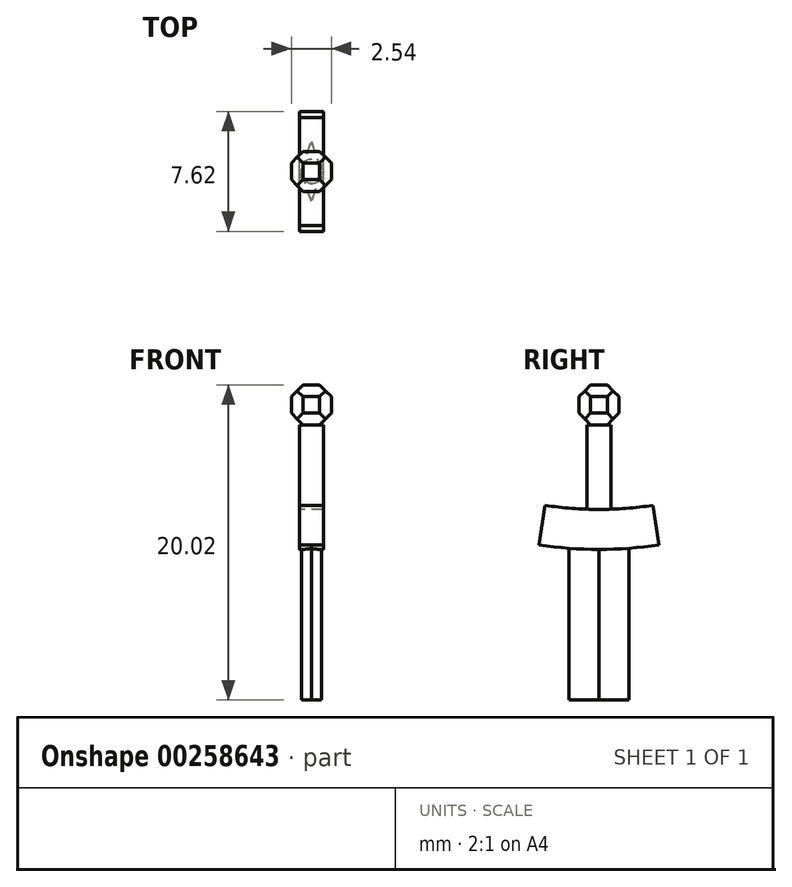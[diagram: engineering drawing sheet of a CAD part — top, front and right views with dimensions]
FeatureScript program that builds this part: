
annotation { "Feature Type Name" : "Feature", "Feature Type Description" : "" }
export const myFeature = defineFeature(function(context is Context, id is Id, definition is map)
    precondition{}
    {
        {
            var Q0;
            Q0=qCreatedBy(makeId("Top.planeOp"),FACE);
            var sketch = newSketch(context, id + "F0", { "sketchPlane" : qUnion([Q0])});
            skCircle(sketch, "E0", {"center": v(0, 0) * mm, "radius": 6.35 * mm});
            skSolve(sketch);
        }
        {
            var Q0;
            Q0=qSketchRegion(id+"F0",true);
            extrude(context, id + "F1", {"entities" : qUnion([Q0]), "depth" : 1.59 * mm});
        }
        {
            var Q0;
            Q0=makeQuery(id+"F1.opExtrude","CAP_FACE",FACE,{"disambiguationData":[OSD([sQuery(id+"F0.wireOp",EDGE,"E0")])],"isStart":false});
            var sketch = newSketch(context, id + "F2", { "sketchPlane" : qUnion([Q0])});
            skCircle(sketch, "E1", {"center": v(0, 0) * mm, "radius": 5.72 * mm});
            skCircle(sketch, "E2.0", {"center": v(0, 0) * mm, "radius": 6.35 * mm});
            skFitSpline(sketch, "E3", {"points": [v(-2.99, -3.48) * mm, v(-2.95, -3.46) * mm, v(-2.86, -3.42) * mm, v(-2.74, -3.39) * mm, v(-2.6, -3.35) * mm, v(-2.43, -3.3) * mm, v(-2.3, -3.28) * mm, v(-2.2, -3.25) * mm, v(-2.15, -3.14) * mm, v(-2.13, -3.01) * mm, v(-2.13, -2.82) * mm, v(-2.12, -2.72) * mm, v(-2.07, -2.57) * mm, v(-2, -2.44) * mm, v(-1.95, -2.43) * mm, v(-1.87, -2.47) * mm, v(-1.8, -2.57) * mm, v(-1.76, -2.65) * mm, v(-1.67, -2.67) * mm, v(-1.54, -2.67) * mm, v(-1.4, -2.63) * mm, v(-1.28, -2.57) * mm, v(-1.17, -2.5) * mm, v(-1.04, -2.4) * mm, v(-0.91, -2.23) * mm, v(-0.83, -2.05) * mm, v(-0.77, -1.87) * mm, v(-0.77, -1.6) * mm, v(-0.82, -1.35) * mm, v(-0.9, -1.14) * mm, v(-1.03, -0.9) * mm, v(-1.19, -0.72) * mm, v(-1.49, -0.53) * mm, v(-1.79, -0.45) * mm, v(-2.09, -0.45) * mm, v(-2.47, -0.46) * mm, v(-2.74, -0.46) * mm, v(-2.94, -0.5) * mm, v(-3.18, -0.62) * mm, v(-3.33, -0.78) * mm, v(-3.4, -0.96) * mm, v(-3.45, -1.13) * mm, v(-3.45, -1.23) * mm, v(-3.5, -1.37) * mm, v(-3.57, -1.5) * mm, v(-3.61, -1.59) * mm, v(-3.6, -1.65) * mm, v(-3.56, -1.72) * mm, v(-3.53, -1.77) * mm, v(-3.51, -1.85) * mm, v(-3.57, -1.93) * mm, v(-3.6, -1.96) * mm, v(-3.66, -2) * mm, v(-3.66, -2.01) * mm, v(-3.67, -2.03) * mm, v(-3.66, -2.05) * mm, v(-3.65, -2.07) * mm, v(-3.63, -2.09) * mm, v(-3.53, -2.23) * mm, v(-3.46, -2.33) * mm, v(-3.48, -2.4) * mm, v(-3.54, -2.44) * mm, v(-3.6, -2.48) * mm, v(-3.61, -2.49) * mm, v(-3.6, -2.5) * mm, v(-3.57, -2.52) * mm, v(-3.56, -2.54) * mm, v(-3.57, -2.57) * mm, v(-3.6, -2.6) * mm, v(-3.65, -2.66) * mm, v(-3.66, -2.72) * mm, v(-3.59, -2.76) * mm, v(-3.44, -2.8) * mm, v(-3.3, -2.78) * mm, v(-3.16, -2.74) * mm, v(-3.02, -2.7) * mm, v(-2.86, -2.69) * mm, v(-2.77, -2.7) * mm, v(-2.74, -2.74) * mm, v(-2.73, -2.81) * mm, v(-2.74, -2.88) * mm, v(-2.78, -2.96) * mm, v(-2.92, -3) * mm, v(-3, -3.03) * mm, v(-3.1, -3.05) * mm, v(-3.29, -3.07) * mm, v(-3.43, -3.07) * mm, v(-3.55, -3.04) * mm, v(-3.62, -3.03) * mm, v(-3.64, -3.06) * mm, v(-3.59, -3.13) * mm, v(-3.56, -3.22) * mm, v(-3.58, -3.3) * mm, v(-3.6, -3.39) * mm, v(-3.6, -3.5) * mm, v(-3.52, -3.56) * mm, v(-3.18, -3.57) * mm, v(-2.99, -3.48) * mm]});
            skFitSpline(sketch, "E4", {"points": [v(-3.38, -1.71) * mm, v(-3.39, -1.8) * mm, v(-3.34, -1.88) * mm, v(-3.3, -1.95) * mm, v(-3.3, -2.01) * mm, v(-3.3, -2.06) * mm, v(-3.26, -2.12) * mm, v(-3.17, -2.1) * mm, v(-3.11, -2) * mm, v(-3.11, -1.92) * mm, v(-3.13, -1.84) * mm, v(-3.19, -1.76) * mm, v(-3.25, -1.72) * mm, v(-3.32, -1.7) * mm, v(-3.38, -1.71) * mm]});
            skLineSegment(sketch, "E5", {"start": v(-3.52, -2.83) * mm, "end": v(-3.52, -2.9) * mm});
            skLineSegment(sketch, "E6", {"start": v(-3.52, -2.9) * mm, "end": v(-3.44, -2.92) * mm});
            skLineSegment(sketch, "E7", {"start": v(-3.44, -2.92) * mm, "end": v(-3.44, -2.85) * mm});
            skLineSegment(sketch, "E8", {"start": v(-3.44, -2.85) * mm, "end": v(-3.52, -2.83) * mm});
            skLineSegment(sketch, "E9", {"start": v(-3.41, -2.85) * mm, "end": v(-3.41, -2.92) * mm});
            skLineSegment(sketch, "E10", {"start": v(-3.41, -2.92) * mm, "end": v(-3.33, -2.92) * mm});
            skLineSegment(sketch, "E11", {"start": v(-3.33, -2.92) * mm, "end": v(-3.33, -2.85) * mm});
            skLineSegment(sketch, "E12", {"start": v(-3.33, -2.85) * mm, "end": v(-3.41, -2.85) * mm});
            skLineSegment(sketch, "E13", {"start": v(-3.3, -2.85) * mm, "end": v(-3.3, -2.92) * mm});
            skLineSegment(sketch, "E14", {"start": v(-3.3, -2.92) * mm, "end": v(-3.22, -2.92) * mm});
            skLineSegment(sketch, "E15", {"start": v(-3.22, -2.92) * mm, "end": v(-3.23, -2.84) * mm});
            skLineSegment(sketch, "E16", {"start": v(-3.23, -2.84) * mm, "end": v(-3.3, -2.85) * mm});
            skLineSegment(sketch, "E17", {"start": v(-3.2, -2.83) * mm, "end": v(-3.2, -2.92) * mm});
            skLineSegment(sketch, "E18", {"start": v(-3.2, -2.92) * mm, "end": v(-3.12, -2.9) * mm});
            skLineSegment(sketch, "E19", {"start": v(-3.12, -2.9) * mm, "end": v(-3.12, -2.81) * mm});
            skLineSegment(sketch, "E20", {"start": v(-3.12, -2.81) * mm, "end": v(-3.2, -2.83) * mm});
            skLineSegment(sketch, "E21", {"start": v(-3.09, -2.8) * mm, "end": v(-3.09, -2.9) * mm});
            skLineSegment(sketch, "E22", {"start": v(-3.09, -2.9) * mm, "end": v(-3, -2.87) * mm});
            skLineSegment(sketch, "E23", {"start": v(-3, -2.87) * mm, "end": v(-3, -2.77) * mm});
            skLineSegment(sketch, "E24", {"start": v(-3, -2.77) * mm, "end": v(-3.09, -2.8) * mm});
            skLineSegment(sketch, "E25", {"start": v(-2.98, -2.75) * mm, "end": v(-2.98, -2.86) * mm});
            skLineSegment(sketch, "E26", {"start": v(-2.98, -2.86) * mm, "end": v(-2.9, -2.83) * mm});
            skLineSegment(sketch, "E27", {"start": v(-2.9, -2.83) * mm, "end": v(-2.9, -2.73) * mm});
            skLineSegment(sketch, "E28", {"start": v(-2.9, -2.73) * mm, "end": v(-2.98, -2.75) * mm});
            skLineSegment(sketch, "E29", {"start": v(-2.87, -2.72) * mm, "end": v(-2.87, -2.81) * mm});
            skLineSegment(sketch, "E30", {"start": v(-2.87, -2.81) * mm, "end": v(-2.77, -2.77) * mm});
            skLineSegment(sketch, "E31", {"start": v(-2.77, -2.8) * mm, "end": v(-2.88, -2.85) * mm});
            skLineSegment(sketch, "E32", {"start": v(-2.88, -2.85) * mm, "end": v(-2.88, -2.94) * mm});
            skLineSegment(sketch, "E33", {"start": v(-2.9, -2.95) * mm, "end": v(-2.9, -2.87) * mm});
            skLineSegment(sketch, "E34", {"start": v(-2.9, -2.87) * mm, "end": v(-2.98, -2.9) * mm});
            skLineSegment(sketch, "E35", {"start": v(-2.98, -2.9) * mm, "end": v(-2.98, -2.97) * mm});
            skLineSegment(sketch, "E36", {"start": v(-2.98, -2.97) * mm, "end": v(-2.9, -2.95) * mm});
            skLineSegment(sketch, "E37", {"start": v(-3, -2.9) * mm, "end": v(-3.09, -2.92) * mm});
            skPoint(sketch, "E37.startSnap0", {"position": v(-3.16, -2.9) * mm});
            skLineSegment(sketch, "E38", {"start": v(-3.09, -2.92) * mm, "end": v(-3.09, -3) * mm});
            skLineSegment(sketch, "E39", {"start": v(-3.09, -3) * mm, "end": v(-3, -2.98) * mm});
            skLineSegment(sketch, "E40", {"start": v(-3, -2.98) * mm, "end": v(-3, -2.9) * mm});
            skLineSegment(sketch, "E41", {"start": v(-3.12, -2.94) * mm, "end": v(-3.2, -2.95) * mm});
            skLineSegment(sketch, "E42", {"start": v(-3.2, -2.95) * mm, "end": v(-3.2, -3.02) * mm});
            skLineSegment(sketch, "E43", {"start": v(-3.2, -3.02) * mm, "end": v(-3.12, -3.01) * mm});
            skLineSegment(sketch, "E44", {"start": v(-3.12, -3.01) * mm, "end": v(-3.12, -2.94) * mm});
            skLineSegment(sketch, "E45", {"start": v(-3.23, -2.95) * mm, "end": v(-3.3, -2.95) * mm});
            skLineSegment(sketch, "E46", {"start": v(-3.3, -2.95) * mm, "end": v(-3.3, -3.03) * mm});
            skLineSegment(sketch, "E47", {"start": v(-3.3, -3.03) * mm, "end": v(-3.23, -3.03) * mm});
            skLineSegment(sketch, "E48", {"start": v(-3.23, -3.03) * mm, "end": v(-3.23, -2.95) * mm});
            skLineSegment(sketch, "E49", {"start": v(-3.33, -2.95) * mm, "end": v(-3.41, -2.95) * mm});
            skLineSegment(sketch, "E50", {"start": v(-3.41, -2.95) * mm, "end": v(-3.41, -3.02) * mm});
            skLineSegment(sketch, "E51", {"start": v(-3.41, -3.02) * mm, "end": v(-3.33, -3.03) * mm});
            skLineSegment(sketch, "E52", {"start": v(-3.33, -3.03) * mm, "end": v(-3.33, -2.95) * mm});
            skLineSegment(sketch, "E53", {"start": v(-3.52, -2.94) * mm, "end": v(-3.44, -2.95) * mm});
            skLineSegment(sketch, "E54", {"start": v(-3.44, -2.95) * mm, "end": v(-3.44, -3.01) * mm});
            skLineSegment(sketch, "E55", {"start": v(-3.44, -3.01) * mm, "end": v(-3.52, -3) * mm});
            skLineSegment(sketch, "E56", {"start": v(-3.52, -3) * mm, "end": v(-3.52, -2.94) * mm});
            skLineSegment(sketch, "E57", {"start": v(-3.64, -2.91) * mm, "end": v(-3.55, -2.94) * mm});
            skLineSegment(sketch, "E58", {"start": v(-3.55, -2.94) * mm, "end": v(-3.55, -3) * mm});
            skLineSegment(sketch, "E59", {"start": v(-3.55, -2.82) * mm, "end": v(-3.55, -2.9) * mm});
            skLineSegment(sketch, "E60", {"start": v(-3.55, -2.9) * mm, "end": v(-3.64, -2.88) * mm});
            skArc(sketch, "E61", {"start": v(-3.55, -2.82) * mm, "mid": v(-3.61, -2.82) * mm, "end": v(-3.64, -2.88) * mm});
            skArc(sketch, "E62", {"start": v(-3.64, -2.91) * mm, "mid": v(-3.61, -2.97) * mm, "end": v(-3.55, -3) * mm});
            skArc(sketch, "E63", {"start": v(-2.77, -2.77) * mm, "mid": v(-2.82, -2.73) * mm, "end": v(-2.87, -2.72) * mm});
            skArc(sketch, "E64", {"start": v(-2.88, -2.94) * mm, "mid": v(-2.8, -2.9) * mm, "end": v(-2.77, -2.8) * mm});
            skFitSpline(sketch, "E65", {"points": [v(2.09, -3.54) * mm, v(2.12, -3.52) * mm, v(2.21, -3.48) * mm, v(2.33, -3.45) * mm, v(2.46, -3.4) * mm, v(2.64, -3.36) * mm, v(2.76, -3.34) * mm, v(2.87, -3.3) * mm, v(2.92, -3.2) * mm, v(2.94, -3.08) * mm, v(2.95, -2.88) * mm, v(2.95, -2.78) * mm, v(3, -2.63) * mm, v(3.08, -2.5) * mm, v(3.13, -2.5) * mm, v(3.2, -2.53) * mm, v(3.27, -2.64) * mm, v(3.31, -2.71) * mm, v(3.4, -2.74) * mm, v(3.53, -2.74) * mm, v(3.67, -2.69) * mm, v(3.8, -2.63) * mm, v(3.9, -2.56) * mm, v(4.03, -2.46) * mm, v(4.16, -2.29) * mm, v(4.24, -2.1) * mm, v(4.3, -1.94) * mm, v(4.3, -1.66) * mm, v(4.25, -1.41) * mm, v(4.18, -1.2) * mm, v(4.04, -0.96) * mm, v(3.89, -0.78) * mm, v(3.58, -0.6) * mm, v(3.29, -0.51) * mm, v(2.97, -0.48) * mm, v(2.59, -0.52) * mm, v(2.33, -0.52) * mm, v(2.13, -0.57) * mm, v(1.9, -0.68) * mm, v(1.74, -0.84) * mm, v(1.67, -1.02) * mm, v(1.62, -1.2) * mm, v(1.63, -1.3) * mm, v(1.57, -1.43) * mm, v(1.5, -1.57) * mm, v(1.46, -1.65) * mm, v(1.46, -1.71) * mm, v(1.51, -1.78) * mm, v(1.54, -1.83) * mm, v(1.56, -1.91) * mm, v(1.5, -1.99) * mm, v(1.46, -2.02) * mm, v(1.41, -2.06) * mm, v(1.4, -2.08) * mm, v(1.4, -2.1) * mm, v(1.4, -2.11) * mm, v(1.42, -2.13) * mm, v(1.44, -2.15) * mm, v(1.54, -2.3) * mm, v(1.61, -2.4) * mm, v(1.6, -2.46) * mm, v(1.53, -2.5) * mm, v(1.47, -2.54) * mm, v(1.46, -2.55) * mm, v(1.48, -2.56) * mm, v(1.5, -2.58) * mm, v(1.52, -2.6) * mm, v(1.5, -2.63) * mm, v(1.47, -2.67) * mm, v(1.43, -2.72) * mm, v(1.41, -2.78) * mm, v(1.49, -2.82) * mm, v(1.63, -2.85) * mm, v(1.77, -2.85) * mm, v(1.91, -2.8) * mm, v(2.05, -2.77) * mm, v(2.21, -2.75) * mm, v(2.3, -2.77) * mm, v(2.33, -2.8) * mm, v(2.35, -2.88) * mm, v(2.33, -2.95) * mm, v(2.29, -3.02) * mm, v(2.15, -3.07) * mm, v(2.07, -3.09) * mm, v(1.97, -3.11) * mm, v(1.79, -3.14) * mm, v(1.64, -3.13) * mm, v(1.52, -3.1) * mm, v(1.45, -3.1) * mm, v(1.43, -3.13) * mm, v(1.48, -3.2) * mm, v(1.51, -3.28) * mm, v(1.5, -3.36) * mm, v(1.48, -3.45) * mm, v(1.48, -3.56) * mm, v(1.55, -3.62) * mm, v(1.9, -3.63) * mm, v(2.09, -3.54) * mm]});
            skFitSpline(sketch, "E66", {"points": [v(1.7, -1.77) * mm, v(1.69, -1.86) * mm, v(1.73, -1.95) * mm, v(1.78, -2) * mm, v(1.78, -2.08) * mm, v(1.76, -2.13) * mm, v(1.8, -2.19) * mm, v(1.9, -2.17) * mm, v(1.96, -2.07) * mm, v(1.96, -1.98) * mm, v(1.95, -1.9) * mm, v(1.88, -1.82) * mm, v(1.82, -1.78) * mm, v(1.75, -1.76) * mm, v(1.7, -1.77) * mm]});
            skLineSegment(sketch, "E67", {"start": v(1.55, -2.9) * mm, "end": v(1.55, -2.97) * mm});
            skLineSegment(sketch, "E68", {"start": v(1.55, -2.97) * mm, "end": v(1.63, -2.98) * mm});
            skLineSegment(sketch, "E69", {"start": v(1.63, -2.98) * mm, "end": v(1.63, -2.9) * mm});
            skLineSegment(sketch, "E70", {"start": v(1.63, -2.9) * mm, "end": v(1.55, -2.9) * mm});
            skLineSegment(sketch, "E71", {"start": v(1.66, -2.91) * mm, "end": v(1.66, -2.98) * mm});
            skLineSegment(sketch, "E72", {"start": v(1.66, -2.98) * mm, "end": v(1.74, -2.98) * mm});
            skLineSegment(sketch, "E73", {"start": v(1.74, -2.98) * mm, "end": v(1.74, -2.92) * mm});
            skLineSegment(sketch, "E74", {"start": v(1.74, -2.92) * mm, "end": v(1.66, -2.91) * mm});
            skLineSegment(sketch, "E75", {"start": v(1.77, -2.91) * mm, "end": v(1.77, -2.98) * mm});
            skLineSegment(sketch, "E76", {"start": v(1.77, -2.98) * mm, "end": v(1.85, -2.98) * mm});
            skLineSegment(sketch, "E77", {"start": v(1.85, -2.98) * mm, "end": v(1.85, -2.9) * mm});
            skLineSegment(sketch, "E78", {"start": v(1.85, -2.9) * mm, "end": v(1.77, -2.91) * mm});
            skLineSegment(sketch, "E79", {"start": v(1.88, -2.9) * mm, "end": v(1.88, -2.98) * mm});
            skLineSegment(sketch, "E80", {"start": v(1.88, -2.98) * mm, "end": v(1.95, -2.96) * mm});
            skLineSegment(sketch, "E81", {"start": v(1.95, -2.96) * mm, "end": v(1.95, -2.88) * mm});
            skLineSegment(sketch, "E82", {"start": v(1.95, -2.88) * mm, "end": v(1.88, -2.9) * mm});
            skLineSegment(sketch, "E83", {"start": v(1.99, -2.86) * mm, "end": v(1.99, -2.96) * mm});
            skLineSegment(sketch, "E84", {"start": v(1.99, -2.96) * mm, "end": v(2.07, -2.93) * mm});
            skLineSegment(sketch, "E85", {"start": v(2.07, -2.93) * mm, "end": v(2.07, -2.83) * mm});
            skLineSegment(sketch, "E86", {"start": v(2.07, -2.83) * mm, "end": v(1.99, -2.86) * mm});
            skLineSegment(sketch, "E87", {"start": v(2.1, -2.82) * mm, "end": v(2.1, -2.92) * mm});
            skLineSegment(sketch, "E88", {"start": v(2.1, -2.92) * mm, "end": v(2.17, -2.9) * mm});
            skLineSegment(sketch, "E89", {"start": v(2.17, -2.9) * mm, "end": v(2.17, -2.8) * mm});
            skLineSegment(sketch, "E90", {"start": v(2.17, -2.8) * mm, "end": v(2.1, -2.82) * mm});
            skLineSegment(sketch, "E91", {"start": v(2.2, -2.79) * mm, "end": v(2.2, -2.88) * mm});
            skLineSegment(sketch, "E92", {"start": v(2.2, -2.88) * mm, "end": v(2.3, -2.84) * mm});
            skLineSegment(sketch, "E93", {"start": v(2.3, -2.87) * mm, "end": v(2.2, -2.92) * mm});
            skLineSegment(sketch, "E94", {"start": v(2.2, -2.92) * mm, "end": v(2.2, -3) * mm});
            skLineSegment(sketch, "E95", {"start": v(2.17, -3.01) * mm, "end": v(2.17, -2.93) * mm});
            skLineSegment(sketch, "E96", {"start": v(2.17, -2.93) * mm, "end": v(2.1, -2.96) * mm});
            skLineSegment(sketch, "E97", {"start": v(2.1, -2.96) * mm, "end": v(2.1, -3.04) * mm});
            skLineSegment(sketch, "E98", {"start": v(2.1, -3.04) * mm, "end": v(2.17, -3.01) * mm});
            skLineSegment(sketch, "E99", {"start": v(2.06, -2.97) * mm, "end": v(1.98, -2.99) * mm});
            skPoint(sketch, "E99.startSnap0", {"position": v(1.91, -2.97) * mm});
            skLineSegment(sketch, "E100", {"start": v(1.98, -2.99) * mm, "end": v(1.99, -3.07) * mm});
            skLineSegment(sketch, "E101", {"start": v(1.99, -3.07) * mm, "end": v(2.07, -3.05) * mm});
            skLineSegment(sketch, "E102", {"start": v(2.07, -3.05) * mm, "end": v(2.06, -2.97) * mm});
            skLineSegment(sketch, "E103", {"start": v(1.95, -3) * mm, "end": v(1.88, -3.01) * mm});
            skLineSegment(sketch, "E104", {"start": v(1.88, -3.01) * mm, "end": v(1.88, -3.09) * mm});
            skLineSegment(sketch, "E105", {"start": v(1.88, -3.09) * mm, "end": v(1.95, -3.07) * mm});
            skLineSegment(sketch, "E106", {"start": v(1.95, -3.07) * mm, "end": v(1.95, -3) * mm});
            skLineSegment(sketch, "E107", {"start": v(1.84, -3.02) * mm, "end": v(1.77, -3.02) * mm});
            skLineSegment(sketch, "E108", {"start": v(1.77, -3.02) * mm, "end": v(1.77, -3.1) * mm});
            skLineSegment(sketch, "E109", {"start": v(1.77, -3.1) * mm, "end": v(1.85, -3.1) * mm});
            skLineSegment(sketch, "E110", {"start": v(1.85, -3.1) * mm, "end": v(1.84, -3.02) * mm});
            skLineSegment(sketch, "E111", {"start": v(1.74, -3.02) * mm, "end": v(1.66, -3.02) * mm});
            skLineSegment(sketch, "E112", {"start": v(1.66, -3.02) * mm, "end": v(1.66, -3.08) * mm});
            skLineSegment(sketch, "E113", {"start": v(1.66, -3.08) * mm, "end": v(1.74, -3.1) * mm});
            skLineSegment(sketch, "E114", {"start": v(1.74, -3.1) * mm, "end": v(1.74, -3.02) * mm});
            skLineSegment(sketch, "E115", {"start": v(1.56, -3) * mm, "end": v(1.63, -3.01) * mm});
            skLineSegment(sketch, "E116", {"start": v(1.63, -3.01) * mm, "end": v(1.63, -3.08) * mm});
            skLineSegment(sketch, "E117", {"start": v(1.63, -3.08) * mm, "end": v(1.55, -3.07) * mm});
            skLineSegment(sketch, "E118", {"start": v(1.55, -3.07) * mm, "end": v(1.56, -3) * mm});
            skLineSegment(sketch, "E119", {"start": v(1.43, -2.97) * mm, "end": v(1.52, -3) * mm});
            skLineSegment(sketch, "E120", {"start": v(1.52, -3) * mm, "end": v(1.52, -3.06) * mm});
            skLineSegment(sketch, "E121", {"start": v(1.52, -2.89) * mm, "end": v(1.52, -2.96) * mm});
            skLineSegment(sketch, "E122", {"start": v(1.52, -2.96) * mm, "end": v(1.43, -2.94) * mm});
            skArc(sketch, "E123", {"start": v(1.52, -2.89) * mm, "mid": v(1.46, -2.88) * mm, "end": v(1.43, -2.94) * mm});
            skArc(sketch, "E124", {"start": v(1.43, -2.97) * mm, "mid": v(1.46, -3.04) * mm, "end": v(1.52, -3.06) * mm});
            skArc(sketch, "E125", {"start": v(2.3, -2.84) * mm, "mid": v(2.26, -2.8) * mm, "end": v(2.2, -2.79) * mm});
            skArc(sketch, "E126", {"start": v(2.2, -3) * mm, "mid": v(2.27, -2.95) * mm, "end": v(2.3, -2.87) * mm});
            skLineSegment(sketch, "E127", {"start": v(-2.47, -0.46) * mm, "end": v(-2.47, 3.73) * mm});
            skLineSegment(sketch, "E128", {"start": v(-2.47, 3.73) * mm, "end": v(2.97, 3.73) * mm});
            skLineSegment(sketch, "E129", {"start": v(2.97, 3.73) * mm, "end": v(2.97, -0.48) * mm});
            skLineSegment(sketch, "E130", {"start": v(-2.09, -0.45) * mm, "end": v(-2.09, 3.35) * mm});
            skLineSegment(sketch, "E131", {"start": v(-2.09, 3.35) * mm, "end": v(2.59, 3.35) * mm});
            skLineSegment(sketch, "E132", {"start": v(2.59, 3.35) * mm, "end": v(2.59, -0.52) * mm});
            skSolve(sketch);
        }
        {
            var Q0;
            Q0=qSketchRegion(id+"F2",true);
            var Q1;
            Q1=makeQuery(id+"F2.imprint","IMPRINT",FACE,{"disambiguationData":[TD([[makeQuery(id+"F2.imprint","IMPRINT",EDGE,{"derivedFrom":sQuery(id+"F2.wireOp",EDGE,"8ff43451-18cf-4e1d-a6c1-207112ed4b83")}),-1.0]])]});
            var Q2;
            {var subQ0=sQuery(id+"F2.wireOp",EDGE,"f0ZndoA6-M2V5-AV1c-evuh-kt5lGmkfnjif");Q2=makeQuery(id+"F2.imprint","IMPRINT",FACE,{"disambiguationData":[TD([[makeQuery(id+"F2.imprint","IMPRINT",EDGE,{"derivedFrom":subQ0}),-1.0]])]});}
            var Q3;
            Q3=makeQuery(id+"F2.imprint","IMPRINT",FACE,{"disambiguationData":[TD([[makeQuery(id+"F2.imprint","IMPRINT",EDGE,{"derivedFrom":sQuery(id+"F2.wireOp",EDGE,"9676f148-d3db-47f1-8d18-ed8e72a81f72")}),-1.0]])]});
            var Q4;
            Q4=makeQuery(id+"F2.imprint","IMPRINT",FACE,{"disambiguationData":[TD([[makeQuery(id+"F2.imprint","IMPRINT",EDGE,{"derivedFrom":sQuery(id+"F2.wireOp",EDGE,"6HFhc678-r75o-y9sA-huqe-qlUwMVaPKWuP")}),-1.0]])]});
            var Q5;
            Q5=makeQuery(id+"F2.imprint","IMPRINT",FACE,{"disambiguationData":[TD([[makeQuery(id+"F2.imprint","IMPRINT",EDGE,{"derivedFrom":sQuery(id+"F2.wireOp",EDGE,"Xs92rVgm-BZGN-NsKB-OARH-R7qVRdKGH7H2")}),-1.0]])]});
            var Q6;
            Q6=makeQuery(id+"F2.imprint","IMPRINT",FACE,{"disambiguationData":[TD([[makeQuery(id+"F2.imprint","IMPRINT",EDGE,{"derivedFrom":sQuery(id+"F2.wireOp",EDGE,"E6WdCPIx-waOx-idA0-XJ1L-eRR6RgLmtCCS")}),-1.0]])]});
            var Q7;
            Q7=makeQuery(id+"F2.imprint","IMPRINT",FACE,{"disambiguationData":[TD([[makeQuery(id+"F2.imprint","IMPRINT",EDGE,{"derivedFrom":sQuery(id+"F2.wireOp",EDGE,"k1KiTlt2-ZZcU-dbgL-0rmk-Dgw59MTWpoCj")}),1.0]])]});
            var Q8;
            Q8=makeQuery(id+"F2.imprint","IMPRINT",FACE,{"disambiguationData":[TD([[makeQuery(id+"F2.imprint","IMPRINT",EDGE,{"derivedFrom":sQuery(id+"F2.wireOp",EDGE,"Z35Rb9R9-Rahv-nOh3-XL17-nKowExZUsZCT")}),1.0]])]});
            var Q9;
            Q9=makeQuery(id+"F2.imprint","IMPRINT",FACE,{"disambiguationData":[TD([[makeQuery(id+"F2.imprint","IMPRINT",EDGE,{"derivedFrom":sQuery(id+"F2.wireOp",EDGE,"Qg5ONqqo-2bfa-kxUG-9bmz-Wc6T9dYv9u8v")}),1.0]])]});
            var Q10;
            Q10=makeQuery(id+"F2.imprint","IMPRINT",FACE,{"disambiguationData":[TD([[makeQuery(id+"F2.imprint","IMPRINT",EDGE,{"derivedFrom":sQuery(id+"F2.wireOp",EDGE,"AjI9mxPJ-XULu-6nMp-z6qf-DJC3dJrP3SV3")}),1.0]])]});
            var Q11;
            Q11=makeQuery(id+"F2.imprint","IMPRINT",FACE,{"disambiguationData":[TD([[makeQuery(id+"F2.imprint","IMPRINT",EDGE,{"derivedFrom":sQuery(id+"F2.wireOp",EDGE,"SVXRag1M-qj8O-Xghp-BRg2-clQjxRkFYdgi")}),1.0]])]});
            var Q12;
            Q12=makeQuery(id+"F2.imprint","IMPRINT",FACE,{"disambiguationData":[TD([[makeQuery(id+"F2.imprint","IMPRINT",EDGE,{"derivedFrom":sQuery(id+"F2.wireOp",EDGE,"QknCvVvT-fZar-JZdj-N9ht-K5PjY9N2CpLl")}),1.0]])]});
            var Q13;
            Q13=makeQuery(id+"F2.imprint","IMPRINT",FACE,{"disambiguationData":[TD([[makeQuery(id+"F2.imprint","IMPRINT",EDGE,{"derivedFrom":sQuery(id+"F2.wireOp",EDGE,"IwH12iTC-POgW-ZuDk-O3qY-x9Lpsw7XAAf3")}),1.0]])]});
            var Q14;
            Q14=makeQuery(id+"F2.imprint","IMPRINT",FACE,{"disambiguationData":[TD([[makeQuery(id+"F2.imprint","IMPRINT",EDGE,{"derivedFrom":sQuery(id+"F2.wireOp",EDGE,"UGZWNjaC-YJYr-0zUO-1gu3-YYbdkgLbKj1s")}),1.0]])]});
            var Q15;
            Q15=makeQuery(id+"F2.imprint","IMPRINT",FACE,{"disambiguationData":[TD([[makeQuery(id+"F2.imprint","IMPRINT",EDGE,{"derivedFrom":sQuery(id+"F2.wireOp",EDGE,"faBvcXIA-NgVa-Zogo-Hth3-byswulnYsCry")}),1.0]])]});
            var Q16;
            Q16=makeQuery(id+"F2.imprint","IMPRINT",FACE,{"disambiguationData":[TD([[makeQuery(id+"F2.imprint","IMPRINT",EDGE,{"derivedFrom":sQuery(id+"F2.wireOp",EDGE,"z3QF5KZu-mklS-Cyfl-OEiK-EEmoJCKWUvB4")}),1.0]])]});
            var Q17;
            Q17=makeQuery(id+"F2.imprint","IMPRINT",FACE,{"disambiguationData":[TD([[makeQuery(id+"F2.imprint","IMPRINT",EDGE,{"derivedFrom":sQuery(id+"F2.wireOp",EDGE,"V2NIJvH9-TtMw-qc9R-an5m-Kvf6aCU9D1Wj")}),1.0]])]});
            var Q18;
            Q18=makeQuery(id+"F2.imprint","IMPRINT",FACE,{"disambiguationData":[TD([[makeQuery(id+"F2.imprint","IMPRINT",EDGE,{"derivedFrom":sQuery(id+"F2.wireOp",EDGE,"QeDBAyft-zymL-5vx5-wYYY-tHA32UShdvIB")}),1.0]])]});
            var Q19;
            Q19=makeQuery(id+"F2.imprint","IMPRINT",FACE,{"disambiguationData":[TD([[makeQuery(id+"F2.imprint","IMPRINT",EDGE,{"derivedFrom":sQuery(id+"F2.wireOp",EDGE,"WRGg1PvO-WrmP-NIcv-oRJx-bzyG9trbOkE2")}),1.0]])]});
            var Q20;
            Q20=makeQuery(id+"F2.imprint","IMPRINT",FACE,{"disambiguationData":[TD([[makeQuery(id+"F2.imprint","IMPRINT",EDGE,{"derivedFrom":sQuery(id+"F2.wireOp",EDGE,"75ec5599-b41b-4d6a-bb06-b73393bb844d")}),-1.0]])]});
            var Q21;
            Q21=makeQuery(id+"F2.imprint","IMPRINT",FACE,{"disambiguationData":[TD([[makeQuery(id+"F2.imprint","IMPRINT",EDGE,{"derivedFrom":sQuery(id+"F2.wireOp",EDGE,"62e6d997-3ff5-4a1c-8de8-b05959ec7cbc")}),-1.0]])]});
            var Q22;
            Q22=makeQuery(id+"F2.imprint","IMPRINT",FACE,{"disambiguationData":[TD([[makeQuery(id+"F2.imprint","IMPRINT",EDGE,{"derivedFrom":sQuery(id+"F2.wireOp",EDGE,"b8f4918c-dbd8-4fdd-af15-bc96a6b6a90d")}),-1.0]])]});
            var Q23;
            Q23=makeQuery(id+"F2.imprint","IMPRINT",FACE,{"disambiguationData":[TD([[makeQuery(id+"F2.imprint","IMPRINT",EDGE,{"derivedFrom":sQuery(id+"F2.wireOp",EDGE,"337819dd-2963-4144-94d7-e260421f4e37")}),1.0]])]});
            var Q24;
            Q24=makeQuery(id+"F2.imprint","IMPRINT",FACE,{"disambiguationData":[TD([[makeQuery(id+"F2.imprint","IMPRINT",EDGE,{"derivedFrom":sQuery(id+"F2.wireOp",EDGE,"19c6ec17-bb67-46df-91db-361c1b9a8fc6")}),1.0]])]});
            var Q25;
            Q25=makeQuery(id+"F2.imprint","IMPRINT",FACE,{"disambiguationData":[TD([[makeQuery(id+"F2.imprint","IMPRINT",EDGE,{"derivedFrom":sQuery(id+"F2.wireOp",EDGE,"b55352ad-c42c-4425-987b-4bb80f046402")}),1.0]])]});
            var Q26;
            Q26=makeQuery(id+"F2.imprint","IMPRINT",FACE,{"disambiguationData":[TD([[makeQuery(id+"F2.imprint","IMPRINT",EDGE,{"derivedFrom":sQuery(id+"F2.wireOp",EDGE,"b27b330e-c63e-4a5d-9a41-1e5f11f57855")}),1.0]])]});
            var Q27;
            Q27=makeQuery(id+"F2.imprint","IMPRINT",FACE,{"disambiguationData":[TD([[makeQuery(id+"F2.imprint","IMPRINT",EDGE,{"derivedFrom":sQuery(id+"F2.wireOp",EDGE,"cd0931f7-213e-4ee0-afb0-8455a1d6fb19")}),1.0]])]});
            var Q28;
            Q28=makeQuery(id+"F2.imprint","IMPRINT",FACE,{"disambiguationData":[TD([[makeQuery(id+"F2.imprint","IMPRINT",EDGE,{"derivedFrom":sQuery(id+"F2.wireOp",EDGE,"2ee7f471-c0e9-471b-9897-f54198c6bebe")}),1.0]])]});
            var Q29;
            Q29=makeQuery(id+"F2.imprint","IMPRINT",FACE,{"disambiguationData":[TD([[makeQuery(id+"F2.imprint","IMPRINT",EDGE,{"derivedFrom":sQuery(id+"F2.wireOp",EDGE,"1a649881-7116-4bcf-9e85-0b71573aa8aa")}),1.0]])]});
            var Q30;
            Q30=makeQuery(id+"F2.imprint","IMPRINT",FACE,{"disambiguationData":[TD([[makeQuery(id+"F2.imprint","IMPRINT",EDGE,{"derivedFrom":sQuery(id+"F2.wireOp",EDGE,"c0ec6f99-1aba-4aca-9953-efef360278b0")}),1.0]])]});
            var Q31;
            Q31=makeQuery(id+"F2.imprint","IMPRINT",FACE,{"disambiguationData":[TD([[makeQuery(id+"F2.imprint","IMPRINT",EDGE,{"derivedFrom":sQuery(id+"F2.wireOp",EDGE,"17c59965-fe3a-40f4-ab79-7e7308dcb645")}),1.0]])]});
            var Q32;
            Q32=makeQuery(id+"F2.imprint","IMPRINT",FACE,{"disambiguationData":[TD([[makeQuery(id+"F2.imprint","IMPRINT",EDGE,{"derivedFrom":sQuery(id+"F2.wireOp",EDGE,"bf3a8e90-f25c-4be5-acd2-482a28ec085b")}),1.0]])]});
            var Q33;
            Q33=makeQuery(id+"F2.imprint","IMPRINT",FACE,{"disambiguationData":[TD([[makeQuery(id+"F2.imprint","IMPRINT",EDGE,{"derivedFrom":sQuery(id+"F2.wireOp",EDGE,"2cfb1138-f32f-4ed4-9923-472279ab65f4")}),1.0]])]});
            var Q34;
            Q34=makeQuery(id+"F2.imprint","IMPRINT",FACE,{"disambiguationData":[TD([[makeQuery(id+"F2.imprint","IMPRINT",EDGE,{"derivedFrom":sQuery(id+"F2.wireOp",EDGE,"cb2b1f7e-f635-4efb-b12c-495075b4995b")}),1.0]])]});
            var Q35;
            Q35=makeQuery(id+"F2.imprint","IMPRINT",FACE,{"disambiguationData":[TD([[makeQuery(id+"F2.imprint","IMPRINT",EDGE,{"derivedFrom":sQuery(id+"F2.wireOp",EDGE,"fe9d17d4-f2a5-44d9-8164-3530e82dfe4b")}),1.0]])]});
            var Q36;
            Q36=makeQuery(id+"F2.imprint","IMPRINT",FACE,{"disambiguationData":[TD([[makeQuery(id+"F2.imprint","IMPRINT",EDGE,{"derivedFrom":sQuery(id+"F2.wireOp",EDGE,"E66")}),-1.0]])]});
            var Q37;
            Q37=makeQuery(id+"F2.imprint","IMPRINT",FACE,{"disambiguationData":[TD([[makeQuery(id+"F2.imprint","IMPRINT",EDGE,{"derivedFrom":sQuery(id+"F2.wireOp",EDGE,"E4")}),-1.0]])]});
            var Q38;
            {var subQ0=sQuery(id+"F2.wireOp",EDGE,"E127");Q38=makeQuery(id+"F2.imprint","IMPRINT",FACE,{"disambiguationData":[TD([[makeQuery(id+"F2.imprint","IMPRINT",EDGE,{"derivedFrom":subQ0}),-1.0]])]});}
            var Q39;
            Q39=makeQuery(id+"F2.imprint","IMPRINT",FACE,{"disambiguationData":[TD([[makeQuery(id+"F2.imprint","IMPRINT",EDGE,{"derivedFrom":sQuery(id+"F2.wireOp",EDGE,"E59")}),-1.0]])]});
            var Q40;
            Q40=makeQuery(id+"F2.imprint","IMPRINT",FACE,{"disambiguationData":[TD([[makeQuery(id+"F2.imprint","IMPRINT",EDGE,{"derivedFrom":sQuery(id+"F2.wireOp",EDGE,"E57")}),-1.0]])]});
            var Q41;
            Q41=makeQuery(id+"F2.imprint","IMPRINT",FACE,{"disambiguationData":[TD([[makeQuery(id+"F2.imprint","IMPRINT",EDGE,{"derivedFrom":sQuery(id+"F2.wireOp",EDGE,"E53")}),-1.0]])]});
            var Q42;
            Q42=makeQuery(id+"F2.imprint","IMPRINT",FACE,{"disambiguationData":[TD([[makeQuery(id+"F2.imprint","IMPRINT",EDGE,{"derivedFrom":sQuery(id+"F2.wireOp",EDGE,"E5")}),1.0]])]});
            var Q43;
            Q43=makeQuery(id+"F2.imprint","IMPRINT",FACE,{"disambiguationData":[TD([[makeQuery(id+"F2.imprint","IMPRINT",EDGE,{"derivedFrom":sQuery(id+"F2.wireOp",EDGE,"E9")}),1.0]])]});
            var Q44;
            Q44=makeQuery(id+"F2.imprint","IMPRINT",FACE,{"disambiguationData":[TD([[makeQuery(id+"F2.imprint","IMPRINT",EDGE,{"derivedFrom":sQuery(id+"F2.wireOp",EDGE,"E49")}),1.0]])]});
            var Q45;
            Q45=makeQuery(id+"F2.imprint","IMPRINT",FACE,{"disambiguationData":[TD([[makeQuery(id+"F2.imprint","IMPRINT",EDGE,{"derivedFrom":sQuery(id+"F2.wireOp",EDGE,"E45")}),1.0]])]});
            var Q46;
            Q46=makeQuery(id+"F2.imprint","IMPRINT",FACE,{"disambiguationData":[TD([[makeQuery(id+"F2.imprint","IMPRINT",EDGE,{"derivedFrom":sQuery(id+"F2.wireOp",EDGE,"E13")}),1.0]])]});
            var Q47;
            Q47=makeQuery(id+"F2.imprint","IMPRINT",FACE,{"disambiguationData":[TD([[makeQuery(id+"F2.imprint","IMPRINT",EDGE,{"derivedFrom":sQuery(id+"F2.wireOp",EDGE,"E17")}),1.0]])]});
            var Q48;
            Q48=makeQuery(id+"F2.imprint","IMPRINT",FACE,{"disambiguationData":[TD([[makeQuery(id+"F2.imprint","IMPRINT",EDGE,{"derivedFrom":sQuery(id+"F2.wireOp",EDGE,"E41")}),1.0]])]});
            var Q49;
            Q49=makeQuery(id+"F2.imprint","IMPRINT",FACE,{"disambiguationData":[TD([[makeQuery(id+"F2.imprint","IMPRINT",EDGE,{"derivedFrom":sQuery(id+"F2.wireOp",EDGE,"E37")}),1.0]])]});
            var Q50;
            Q50=makeQuery(id+"F2.imprint","IMPRINT",FACE,{"disambiguationData":[TD([[makeQuery(id+"F2.imprint","IMPRINT",EDGE,{"derivedFrom":sQuery(id+"F2.wireOp",EDGE,"E21")}),1.0]])]});
            var Q51;
            Q51=makeQuery(id+"F2.imprint","IMPRINT",FACE,{"disambiguationData":[TD([[makeQuery(id+"F2.imprint","IMPRINT",EDGE,{"derivedFrom":sQuery(id+"F2.wireOp",EDGE,"E25")}),1.0]])]});
            var Q52;
            Q52=makeQuery(id+"F2.imprint","IMPRINT",FACE,{"disambiguationData":[TD([[makeQuery(id+"F2.imprint","IMPRINT",EDGE,{"derivedFrom":sQuery(id+"F2.wireOp",EDGE,"E33")}),1.0]])]});
            var Q53;
            Q53=makeQuery(id+"F2.imprint","IMPRINT",FACE,{"disambiguationData":[TD([[makeQuery(id+"F2.imprint","IMPRINT",EDGE,{"derivedFrom":sQuery(id+"F2.wireOp",EDGE,"E31")}),1.0]])]});
            var Q54;
            Q54=makeQuery(id+"F2.imprint","IMPRINT",FACE,{"disambiguationData":[TD([[makeQuery(id+"F2.imprint","IMPRINT",EDGE,{"derivedFrom":sQuery(id+"F2.wireOp",EDGE,"E29")}),1.0]])]});
            var Q55;
            Q55=makeQuery(id+"F2.imprint","IMPRINT",FACE,{"disambiguationData":[TD([[makeQuery(id+"F2.imprint","IMPRINT",EDGE,{"derivedFrom":sQuery(id+"F2.wireOp",EDGE,"E91")}),1.0]])]});
            var Q56;
            Q56=makeQuery(id+"F2.imprint","IMPRINT",FACE,{"disambiguationData":[TD([[makeQuery(id+"F2.imprint","IMPRINT",EDGE,{"derivedFrom":sQuery(id+"F2.wireOp",EDGE,"E93")}),1.0]])]});
            var Q57;
            Q57=makeQuery(id+"F2.imprint","IMPRINT",FACE,{"disambiguationData":[TD([[makeQuery(id+"F2.imprint","IMPRINT",EDGE,{"derivedFrom":sQuery(id+"F2.wireOp",EDGE,"E95")}),1.0]])]});
            var Q58;
            Q58=makeQuery(id+"F2.imprint","IMPRINT",FACE,{"disambiguationData":[TD([[makeQuery(id+"F2.imprint","IMPRINT",EDGE,{"derivedFrom":sQuery(id+"F2.wireOp",EDGE,"E87")}),1.0]])]});
            var Q59;
            Q59=makeQuery(id+"F2.imprint","IMPRINT",FACE,{"disambiguationData":[TD([[makeQuery(id+"F2.imprint","IMPRINT",EDGE,{"derivedFrom":sQuery(id+"F2.wireOp",EDGE,"E83")}),1.0]])]});
            var Q60;
            Q60=makeQuery(id+"F2.imprint","IMPRINT",FACE,{"disambiguationData":[TD([[makeQuery(id+"F2.imprint","IMPRINT",EDGE,{"derivedFrom":sQuery(id+"F2.wireOp",EDGE,"E99")}),1.0]])]});
            var Q61;
            Q61=makeQuery(id+"F2.imprint","IMPRINT",FACE,{"disambiguationData":[TD([[makeQuery(id+"F2.imprint","IMPRINT",EDGE,{"derivedFrom":sQuery(id+"F2.wireOp",EDGE,"E103")}),1.0]])]});
            var Q62;
            Q62=makeQuery(id+"F2.imprint","IMPRINT",FACE,{"disambiguationData":[TD([[makeQuery(id+"F2.imprint","IMPRINT",EDGE,{"derivedFrom":sQuery(id+"F2.wireOp",EDGE,"E79")}),1.0]])]});
            var Q63;
            Q63=makeQuery(id+"F2.imprint","IMPRINT",FACE,{"disambiguationData":[TD([[makeQuery(id+"F2.imprint","IMPRINT",EDGE,{"derivedFrom":sQuery(id+"F2.wireOp",EDGE,"E75")}),1.0]])]});
            var Q64;
            Q64=makeQuery(id+"F2.imprint","IMPRINT",FACE,{"disambiguationData":[TD([[makeQuery(id+"F2.imprint","IMPRINT",EDGE,{"derivedFrom":sQuery(id+"F2.wireOp",EDGE,"E107")}),1.0]])]});
            var Q65;
            Q65=makeQuery(id+"F2.imprint","IMPRINT",FACE,{"disambiguationData":[TD([[makeQuery(id+"F2.imprint","IMPRINT",EDGE,{"derivedFrom":sQuery(id+"F2.wireOp",EDGE,"E111")}),1.0]])]});
            var Q66;
            Q66=makeQuery(id+"F2.imprint","IMPRINT",FACE,{"disambiguationData":[TD([[makeQuery(id+"F2.imprint","IMPRINT",EDGE,{"derivedFrom":sQuery(id+"F2.wireOp",EDGE,"E71")}),1.0]])]});
            var Q67;
            Q67=makeQuery(id+"F2.imprint","IMPRINT",FACE,{"disambiguationData":[TD([[makeQuery(id+"F2.imprint","IMPRINT",EDGE,{"derivedFrom":sQuery(id+"F2.wireOp",EDGE,"E67")}),1.0]])]});
            var Q68;
            Q68=makeQuery(id+"F2.imprint","IMPRINT",FACE,{"disambiguationData":[TD([[makeQuery(id+"F2.imprint","IMPRINT",EDGE,{"derivedFrom":sQuery(id+"F2.wireOp",EDGE,"E115")}),-1.0]])]});
            var Q69;
            Q69=makeQuery(id+"F2.imprint","IMPRINT",FACE,{"disambiguationData":[TD([[makeQuery(id+"F2.imprint","IMPRINT",EDGE,{"derivedFrom":sQuery(id+"F2.wireOp",EDGE,"E119")}),-1.0]])]});
            var Q70;
            Q70=makeQuery(id+"F2.imprint","IMPRINT",FACE,{"disambiguationData":[TD([[makeQuery(id+"F2.imprint","IMPRINT",EDGE,{"derivedFrom":sQuery(id+"F2.wireOp",EDGE,"E121")}),-1.0]])]});
            extrude(context, id + "F3", {"entities" : qUnion([Q0, Q1, Q2, Q3, Q4, Q5, Q6, Q7, Q8, Q9, Q10, Q11, Q12, Q13, Q14, Q15, Q16, Q17, Q18, Q19, Q20, Q21, Q22, Q23, Q24, Q25, Q26, Q27, Q28, Q29, Q30, Q31, Q32, Q33, Q34, Q35, Q36, Q37, Q38, Q39, Q40, Q41, Q42, Q43, Q44, Q45, Q46, Q47, Q48, Q49, Q50, Q51, Q52, Q53, Q54, Q55, Q56, Q57, Q58, Q59, Q60, Q61, Q62, Q63, Q64, Q65, Q66, Q67, Q68, Q69, Q70]), "operationType" : NewBodyOperationType.ADD, "depth" : 0.8 * mm});
        }
        {
            var Q0;
            Q0=makeQuery(id+"F3.boolean.opBoolean","SPLIT",FACE,{"disambiguationData":[TD([makeQuery(id+"F3.opExtrude","SWEPT_FACE",FACE,{"disambiguationData":[OSD([sQuery(id+"F2.wireOp",EDGE,"E1")])]})])],"derivedFrom":makeQuery(id+"F1.opExtrude","CAP_FACE",FACE,{"disambiguationData":[OSD([sQuery(id+"F0.wireOp",EDGE,"E0")])],"isStart":false})});
            var sketch = newSketch(context, id + "F4", { "sketchPlane" : qUnion([Q0])});
            skLineSegment(sketch, "E133", {"start": v(0, 1.9) * mm, "end": v(-0.64, 0) * mm});
            skLineSegment(sketch, "E134", {"start": v(-0.64, 0) * mm, "end": v(0, -1.9) * mm});
            skLineSegment(sketch, "E135", {"start": v(0, -1.9) * mm, "end": v(0.64, 0) * mm});
            skLineSegment(sketch, "E136", {"start": v(0.64, 0) * mm, "end": v(0, 1.9) * mm});
            skSolve(sketch);
        }
        {
            var Q0;
            Q0=qSketchRegion(id+"F4",true);
            extrude(context, id + "F5", {"entities" : qUnion([Q0]), "operationType" : NewBodyOperationType.ADD, "depth" : 12.7 * mm});
        }
        {
            var Q0;
            Q0=qCreatedBy(makeId("Right.planeOp"),FACE);
            var sketch = newSketch(context, id + "F6", { "sketchPlane" : qUnion([Q0])});
            skArc(sketch, "E137", {"start": v(3.8, 13.97) * mm, "mid": v(0, 13.68) * mm, "end": v(-3.8, 13.97) * mm});
            skArc(sketch, "E138.0", {"start": v(3.43, 16.48) * mm, "mid": v(0, 16.22) * mm, "end": v(-3.43, 16.48) * mm});
            skLineSegment(sketch, "E139", {"start": v(3.8, 13.97) * mm, "end": v(3.43, 16.48) * mm});
            skLineSegment(sketch, "E140", {"start": v(-3.43, 16.48) * mm, "end": v(-3.8, 13.97) * mm});
            skSolve(sketch);
        }
        {
            var Q0;
            Q0=qSketchRegion(id+"F6",true);
            extrude(context, id + "F7", {"entities" : qUnion([Q0]), "operationType" : NewBodyOperationType.ADD, "endBound" : BoundingType.SYMMETRIC, "depth" : 1.52 * mm});
        }
        {
            var Q0;
            Q0=qCreatedBy(makeId("Right.planeOp"),FACE);
            var sketch = newSketch(context, id + "F8", { "sketchPlane" : qUnion([Q0])});
            skLineSegment(sketch, "E141", {"start": v(0, 13.97) * mm, "end": v(0, 21.6) * mm});
            skLineSegment(sketch, "E142", {"start": v(0, 21.6) * mm, "end": v(0.76, 21.6) * mm});
            skLineSegment(sketch, "E143", {"start": v(0.76, 21.6) * mm, "end": v(0.76, 13.97) * mm});
            skLineSegment(sketch, "E144", {"start": v(0.76, 13.97) * mm, "end": v(0, 13.97) * mm});
            skSolve(sketch);
        }
        {
            var Q0;
            Q0=qSketchRegion(id+"F8",true);
            var Q1;
            Q1=sQuery(id+"F8.wireOp",EDGE,"E141");
            revolve(context, id + "F9", {"operationType" : NewBodyOperationType.ADD, "entities" : qUnion([Q0]), "axis" : qUnion([Q1]), "revolveType" : RevolveType.FULL});
        }
        {
            var Q0;
            Q0=makeQuery(id+"F9.opRevolve","SWEPT_FACE",FACE,{"disambiguationData":[OSD([sQuery(id+"F8.wireOp",EDGE,"E142")])]});
            var sketch = newSketch(context, id + "F10", { "sketchPlane" : qUnion([Q0])});
            skCircle(sketch, "E145.cCircle", {"center": v(0, 0) * mm, "radius": 1.27 * mm, "construction": true});
            skLineSegment(sketch, "E145.0", {"start": v(0.53, -1.27) * mm, "end": v(-0.53, -1.27) * mm});
            skLineSegment(sketch, "E145.1", {"start": v(-0.53, -1.27) * mm, "end": v(-1.27, -0.53) * mm});
            skLineSegment(sketch, "E145.2", {"start": v(-1.27, -0.53) * mm, "end": v(-1.27, 0.53) * mm});
            skLineSegment(sketch, "E145.3", {"start": v(-1.27, 0.53) * mm, "end": v(-0.53, 1.27) * mm});
            skLineSegment(sketch, "E145.4", {"start": v(-0.53, 1.27) * mm, "end": v(0.53, 1.27) * mm});
            skLineSegment(sketch, "E145.5", {"start": v(0.53, 1.27) * mm, "end": v(1.27, 0.53) * mm});
            skLineSegment(sketch, "E145.6", {"start": v(1.27, 0.53) * mm, "end": v(1.27, -0.53) * mm});
            skLineSegment(sketch, "E145.7", {"start": v(1.27, -0.53) * mm, "end": v(0.53, -1.27) * mm});
            skPoint(sketch, "E145.0.midPoint", {"position": v(0, -1.27) * mm});
            skSolve(sketch);
        }
        {
            var Q0;
            Q0=qSketchRegion(id+"F10",true);
            extrude(context, id + "F11", {"entities" : qUnion([Q0]), "operationType" : NewBodyOperationType.ADD, "depth" : 2.54 * mm});
        }
        {
            var Q0;
            Q0=makeQuery(id+"F11.opExtrude","SWEPT_FACE",FACE,{"disambiguationData":[OSD([sQuery(id+"F10.wireOp",EDGE,"E145.6")])]});
            var sketch = newSketch(context, id + "F12", { "sketchPlane" : qUnion([Q0])});
            skCircle(sketch, "E146.cCircle", {"center": v(0, 22.86) * mm, "radius": 1.27 * mm, "construction": true});
            skLineSegment(sketch, "E146.0", {"start": v(-0.53, 24.13) * mm, "end": v(0.53, 24.13) * mm});
            skLineSegment(sketch, "E146.1", {"start": v(0.53, 24.13) * mm, "end": v(1.27, 23.39) * mm});
            skLineSegment(sketch, "E146.2", {"start": v(1.27, 23.39) * mm, "end": v(1.27, 22.33) * mm});
            skLineSegment(sketch, "E146.3", {"start": v(1.27, 22.33) * mm, "end": v(0.53, 21.6) * mm});
            skLineSegment(sketch, "E146.4", {"start": v(0.53, 21.6) * mm, "end": v(-0.53, 21.6) * mm});
            skLineSegment(sketch, "E146.5", {"start": v(-0.53, 21.6) * mm, "end": v(-1.27, 22.33) * mm});
            skLineSegment(sketch, "E146.6", {"start": v(-1.27, 22.33) * mm, "end": v(-1.27, 23.39) * mm});
            skLineSegment(sketch, "E146.7", {"start": v(-1.27, 23.39) * mm, "end": v(-0.53, 24.13) * mm});
            skPoint(sketch, "E146.0.midPoint", {"position": v(0, 24.13) * mm});
            skLineSegment(sketch, "E147.bottom", {"start": v(-1.27, 21.6) * mm, "end": v(1.27, 21.6) * mm});
            skLineSegment(sketch, "E147.top", {"start": v(-1.27, 24.13) * mm, "end": v(1.27, 24.13) * mm});
            skLineSegment(sketch, "E147.left", {"start": v(-1.27, 21.6) * mm, "end": v(-1.27, 24.13) * mm});
            skLineSegment(sketch, "E147.right", {"start": v(1.27, 21.6) * mm, "end": v(1.27, 24.13) * mm});
            skSolve(sketch);
        }
        {
            var Q0;
            {var subQ0=sQuery(id+"F12.wireOp",EDGE,"E146.3");Q0=makeQuery(id+"F12.imprint","IMPRINT",FACE,{"disambiguationData":[TD([[makeQuery(id+"F12.imprint","IMPRINT",EDGE,{"derivedFrom":subQ0}),1.0]])]});}
            var Q1;
            {var subQ0=sQuery(id+"F12.wireOp",EDGE,"E146.5");Q1=makeQuery(id+"F12.imprint","IMPRINT",FACE,{"disambiguationData":[TD([[makeQuery(id+"F12.imprint","IMPRINT",EDGE,{"derivedFrom":subQ0}),1.0]])]});}
            var Q2;
            {var subQ0=sQuery(id+"F12.wireOp",EDGE,"E146.7");Q2=makeQuery(id+"F12.imprint","IMPRINT",FACE,{"disambiguationData":[TD([[makeQuery(id+"F12.imprint","IMPRINT",EDGE,{"derivedFrom":subQ0}),1.0]])]});}
            var Q3;
            {var subQ0=sQuery(id+"F12.wireOp",EDGE,"E146.1");Q3=makeQuery(id+"F12.imprint","IMPRINT",FACE,{"disambiguationData":[TD([[makeQuery(id+"F12.imprint","IMPRINT",EDGE,{"derivedFrom":subQ0}),1.0]])]});}
            extrude(context, id + "F13", {"entities" : qUnion([Q0, Q1, Q2, Q3]), "operationType" : NewBodyOperationType.REMOVE, "oppositeDirection" : true, "depth" : 25.4 * mm});
        }
        {
            var Q0;
            Q0=makeQuery(id+"F11.opExtrude","SWEPT_FACE",FACE,{"disambiguationData":[OSD([sQuery(id+"F10.wireOp",EDGE,"E145.0")])]});
            var sketch = newSketch(context, id + "F14", { "sketchPlane" : qUnion([Q0])});
            skCircle(sketch, "E148.cCircle", {"center": v(0, 22.86) * mm, "radius": 1.27 * mm, "construction": true});
            skPoint(sketch, "E148.cCircle.centerSnap0", {"position": v(0.53, 22.86) * mm});
            skLineSegment(sketch, "E148.0", {"start": v(1.27, 23.39) * mm, "end": v(1.27, 22.33) * mm});
            skLineSegment(sketch, "E148.1", {"start": v(1.27, 22.33) * mm, "end": v(0.53, 21.6) * mm});
            skLineSegment(sketch, "E148.2", {"start": v(0.53, 21.6) * mm, "end": v(-0.53, 21.6) * mm});
            skLineSegment(sketch, "E148.3", {"start": v(-0.53, 21.6) * mm, "end": v(-1.27, 22.33) * mm});
            skLineSegment(sketch, "E148.4", {"start": v(-1.27, 22.33) * mm, "end": v(-1.27, 23.39) * mm});
            skLineSegment(sketch, "E148.5", {"start": v(-1.27, 23.39) * mm, "end": v(-0.53, 24.13) * mm});
            skLineSegment(sketch, "E148.6", {"start": v(-0.53, 24.13) * mm, "end": v(0.53, 24.13) * mm});
            skLineSegment(sketch, "E148.7", {"start": v(0.53, 24.13) * mm, "end": v(1.27, 23.39) * mm});
            skPoint(sketch, "E148.0.midPoint", {"position": v(1.27, 22.86) * mm});
            skLineSegment(sketch, "E149.bottom", {"start": v(-1.27, 21.6) * mm, "end": v(1.27, 21.6) * mm});
            skLineSegment(sketch, "E149.top", {"start": v(-1.27, 24.13) * mm, "end": v(1.27, 24.13) * mm});
            skLineSegment(sketch, "E149.left", {"start": v(-1.27, 21.6) * mm, "end": v(-1.27, 24.13) * mm});
            skLineSegment(sketch, "E149.right", {"start": v(1.27, 21.6) * mm, "end": v(1.27, 24.13) * mm});
            skSolve(sketch);
        }
        {
            var Q0;
            {var subQ0=sQuery(id+"F14.wireOp",EDGE,"E148.1");Q0=makeQuery(id+"F14.imprint","IMPRINT",FACE,{"disambiguationData":[TD([[makeQuery(id+"F14.imprint","IMPRINT",EDGE,{"derivedFrom":subQ0}),1.0]])]});}
            var Q1;
            {var subQ0=sQuery(id+"F14.wireOp",EDGE,"E148.3");Q1=makeQuery(id+"F14.imprint","IMPRINT",FACE,{"disambiguationData":[TD([[makeQuery(id+"F14.imprint","IMPRINT",EDGE,{"derivedFrom":subQ0}),1.0]])]});}
            var Q2;
            {var subQ0=sQuery(id+"F14.wireOp",EDGE,"E148.5");Q2=makeQuery(id+"F14.imprint","IMPRINT",FACE,{"disambiguationData":[TD([[makeQuery(id+"F14.imprint","IMPRINT",EDGE,{"derivedFrom":subQ0}),1.0]])]});}
            var Q3;
            {var subQ0=sQuery(id+"F14.wireOp",EDGE,"E148.7");Q3=makeQuery(id+"F14.imprint","IMPRINT",FACE,{"disambiguationData":[TD([[makeQuery(id+"F14.imprint","IMPRINT",EDGE,{"derivedFrom":subQ0}),1.0]])]});}
            extrude(context, id + "F15", {"entities" : qUnion([Q0, Q1, Q2, Q3]), "operationType" : NewBodyOperationType.REMOVE, "endBound" : BoundingType.THROUGH_ALL, "oppositeDirection" : true, "depth" : 25.4 * mm});
        }
        {
            var Q0;
            Q0=makeQuery(id+"F7.opExtrude","CAP_FACE",FACE,{"disambiguationData":[OSD([sQuery(id+"F6.wireOp",EDGE,"E137"),sQuery(id+"F6.wireOp",EDGE,"E138.0"),sQuery(id+"F6.wireOp",EDGE,"E139"),sQuery(id+"F6.wireOp",EDGE,"E140")])],"isStart":false});
            var sketch = newSketch(context, id + "F16", { "sketchPlane" : qUnion([Q0])});
            skLineSegment(sketch, "E150.bottom", {"start": v(-8.64, 4.11) * mm, "end": v(16.27, 4.11) * mm});
            skLineSegment(sketch, "E150.top", {"start": v(-8.64, -2.9) * mm, "end": v(16.27, -2.9) * mm});
            skLineSegment(sketch, "E150.left", {"start": v(-8.64, 4.11) * mm, "end": v(-8.64, -2.9) * mm});
            skLineSegment(sketch, "E150.right", {"start": v(16.27, 4.11) * mm, "end": v(16.27, -2.9) * mm});
            skSolve(sketch);
        }
        {
            var Q0;
            Q0 = qSketchRegion(id + "F16", true);
            extrude(context, id + "F17", {"entities" : qUnion([Q0]), "operationType" : NewBodyOperationType.REMOVE, "endBound" : BoundingType.SYMMETRIC, "oppositeDirection" : true, "depth" : 25.4 * mm});
        }
    });
